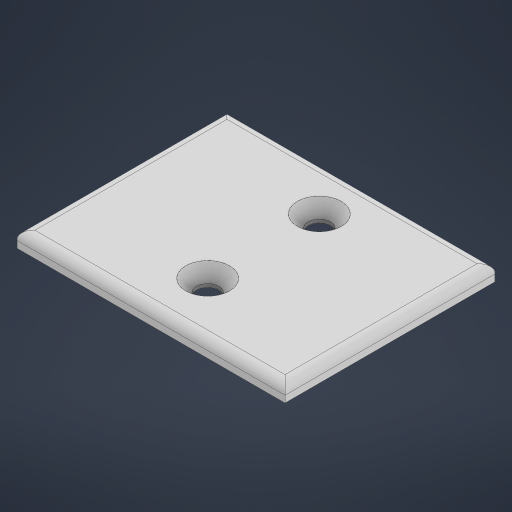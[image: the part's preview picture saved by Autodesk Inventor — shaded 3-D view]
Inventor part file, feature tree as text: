
AUTODESK INVENTOR PART (.ipt)
format: ipt  version: 2024 (Build 280153000, 153)  size: 195,584 bytes
history: native  units: in
note: dims shown in document units (in); Inventor stores cm internally (conversion verified against a paired STEP export)
features: sketch x2, extrude x1, hole x1, fillet x1
ambient origin geometry x8: Origin, YZ Plane, XZ Plane, XY Plane, X Axis, Y Axis, Z Axis, Center Point
bodies: Solid1 (feature_tree)
feature tree (5):
  extrude  "Extrusion1"  Depth=1.8504in
  hole  "Hole1"  [1 undecoded]
  fillet  "Fillet2"  Radius=0.4724in
  sketch  "Sketch1"  dims[d0=2.3622in d1=1.8504in]
  sketch  "Sketch2"  dims[d7=0.1378in d8=0.0in d10=0.9843in d11=0.4724in d12=0.3937in d13=0.196in d14=0.2362in d15=0.385in d16=0.0787in d17=0.5635in d18=0.315in d19=0.8108in d20=0.0787in]
note: 1 required parameter value undecoded (feature->parameter linkage not recoverable at this tier; creation-order binding heuristic only, values carry confidence <= 0.55)
